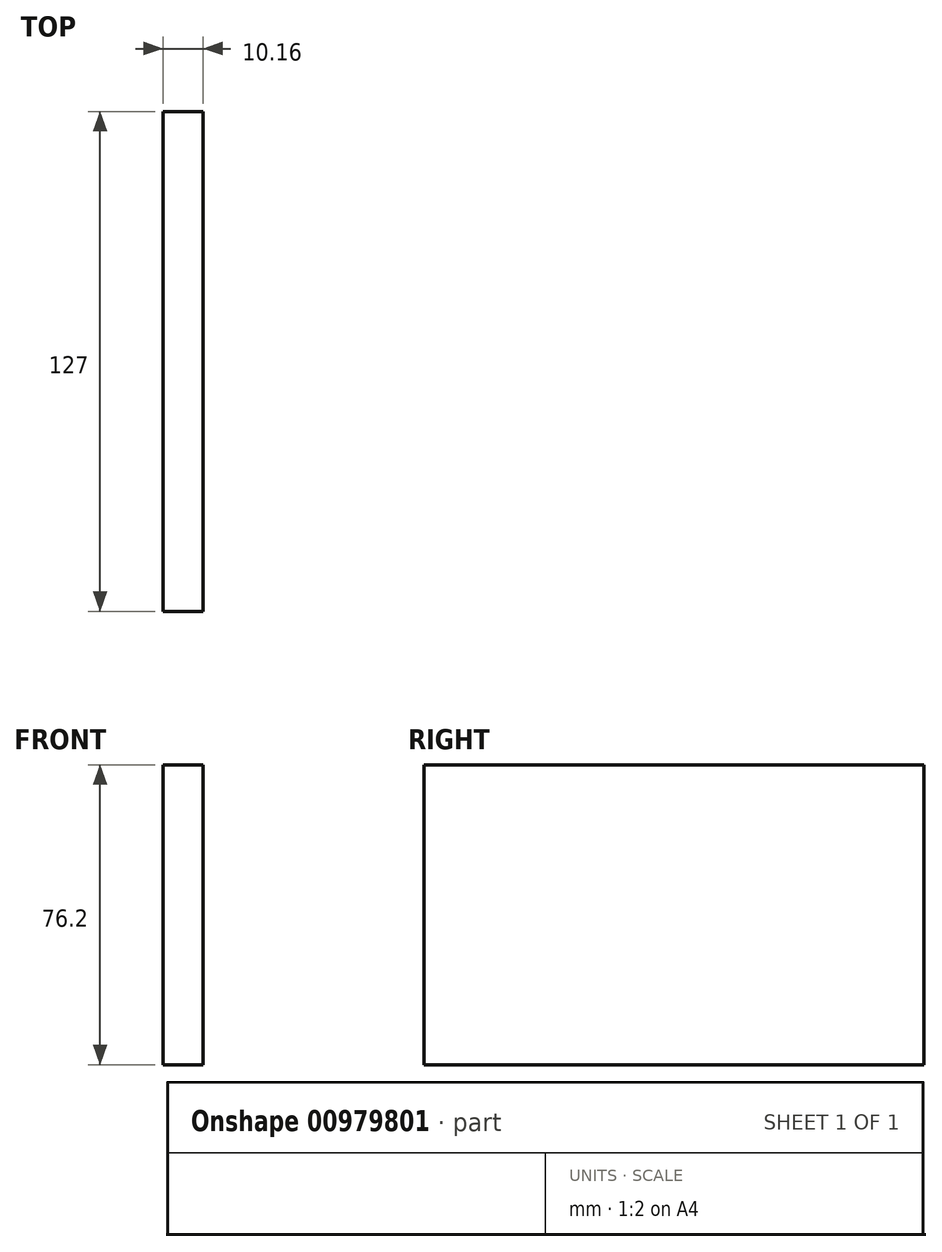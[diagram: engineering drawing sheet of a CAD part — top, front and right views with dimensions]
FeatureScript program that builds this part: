
annotation { "Feature Type Name" : "Feature", "Feature Type Description" : "" }
export const myFeature = defineFeature(function(context is Context, id is Id, definition is map)
    precondition{}
    {
        {
            var Q0;
            Q0=qCreatedBy(makeId("Right.planeOp"),FACE);
            var sketch = newSketch(context, id + "F0", { "sketchPlane" : qUnion([Q0])});
            skLineSegment(sketch, "E0.bottom", {"start": v(-63.5, 38.1) * mm, "end": v(63.5, 38.1) * mm});
            skLineSegment(sketch, "E0.top", {"start": v(-63.5, -38.1) * mm, "end": v(63.5, -38.1) * mm});
            skLineSegment(sketch, "E0.left", {"start": v(-63.5, 38.1) * mm, "end": v(-63.5, -38.1) * mm});
            skLineSegment(sketch, "E0.right", {"start": v(63.5, 38.1) * mm, "end": v(63.5, -38.1) * mm});
            skPoint(sketch, "E0.middle", {"position": v(0, 0) * mm});
            skSolve(sketch);
        }
        {
            var Q0;
            Q0 = qSketchRegion(id + "F0", true);
            extrude(context, id + "F1", {"entities" : qUnion([Q0]), "depth" : 10.16 * mm, "offsetDistance" : 25.4 * mm});
        }
    });
